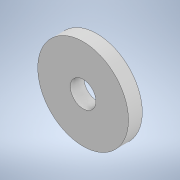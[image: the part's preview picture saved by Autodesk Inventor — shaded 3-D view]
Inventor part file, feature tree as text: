
AUTODESK INVENTOR PART (.ipt)
format: ipt  version: 2022 (Build 260153000, 153)  size: 108,032 bytes
history: native  units: in
note: dims shown in document units (in); Inventor stores cm internally (conversion verified against a paired STEP export)
features: extrude x1, sketch x1
ambient origin geometry x8: Origin, YZ Plane, XZ Plane, XY Plane, X Axis, Y Axis, Z Axis, Center Point
bodies: Body1 (feature_tree)
feature tree (2):
  extrude  "Extrusion1"  TaperAngle=0.0deg  [1 undecoded]
  sketch  "Sketch2"  dims[d0=0.1378in d1=0.0in d2=0.2559in]
note: 1 required parameter value undecoded (feature->parameter linkage not recoverable at this tier; creation-order binding heuristic only, values carry confidence <= 0.55)
